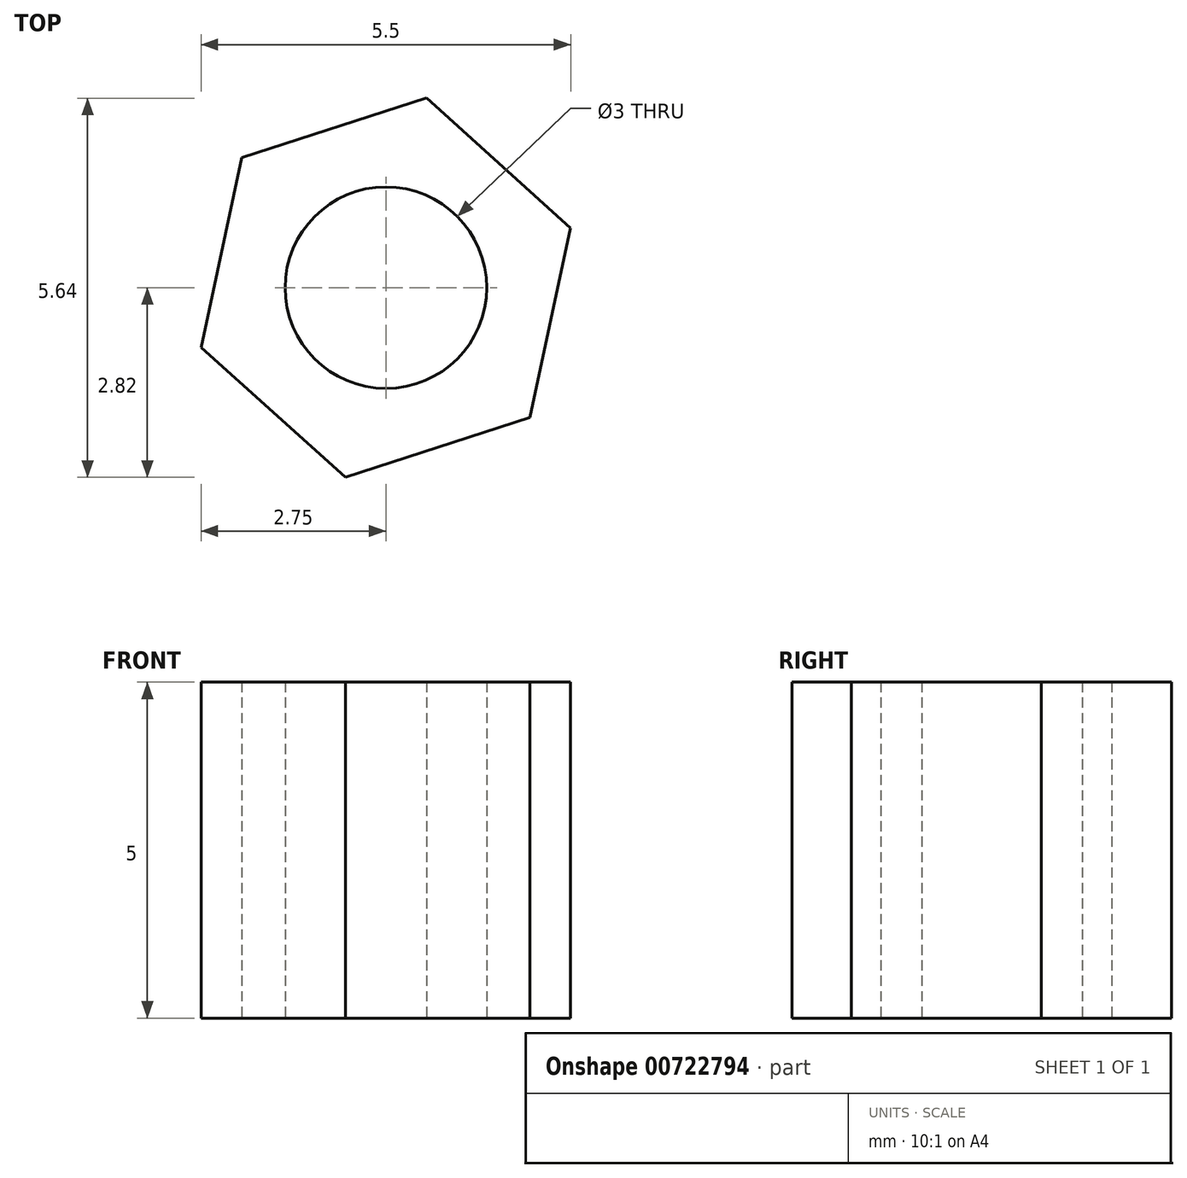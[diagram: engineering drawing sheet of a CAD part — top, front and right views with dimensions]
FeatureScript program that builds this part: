
annotation { "Feature Type Name" : "Feature", "Feature Type Description" : "" }
export const myFeature = defineFeature(function(context is Context, id is Id, definition is map)
    precondition{}
    {
        {
            var Q0;
            Q0=qCreatedBy(makeId("Top.planeOp"),FACE);
            var sketch = newSketch(context, id + "F0", { "sketchPlane" : qUnion([Q0])});
            skCircle(sketch, "E0.cCircle", {"center": v(0, 0) * mm, "radius": 2.5 * mm, "construction": true});
            skLineSegment(sketch, "E0.0", {"start": v(2.75, 0.89) * mm, "end": v(2.14, -1.93) * mm});
            skLineSegment(sketch, "E0.1", {"start": v(2.14, -1.93) * mm, "end": v(-0.6, -2.82) * mm});
            skLineSegment(sketch, "E0.2", {"start": v(-0.6, -2.82) * mm, "end": v(-2.75, -0.89) * mm});
            skLineSegment(sketch, "E0.3", {"start": v(-2.75, -0.89) * mm, "end": v(-2.14, 1.93) * mm});
            skLineSegment(sketch, "E0.4", {"start": v(-2.14, 1.93) * mm, "end": v(0.6, 2.82) * mm});
            skLineSegment(sketch, "E0.5", {"start": v(0.6, 2.82) * mm, "end": v(2.75, 0.89) * mm});
            skPoint(sketch, "E0.0.midPoint", {"position": v(2.44, -0.52) * mm});
            skCircle(sketch, "E1", {"center": v(0, 0) * mm, "radius": 1.5 * mm});
            skSolve(sketch);
        }
        {
            var Q0;
            Q0=makeQuery(id+"F0.imprint","IMPRINT",FACE,{"disambiguationData":[TD([[makeQuery(id+"F0.imprint","IMPRINT",EDGE,{"derivedFrom":sQuery(id+"F0.wireOp",EDGE,"E0.0")}),-1.0]])]});
            extrude(context, id + "F1", {"entities" : qUnion([Q0]), "depth" : 5 * mm, "offsetDistance" : 25 * mm});
        }
    });
